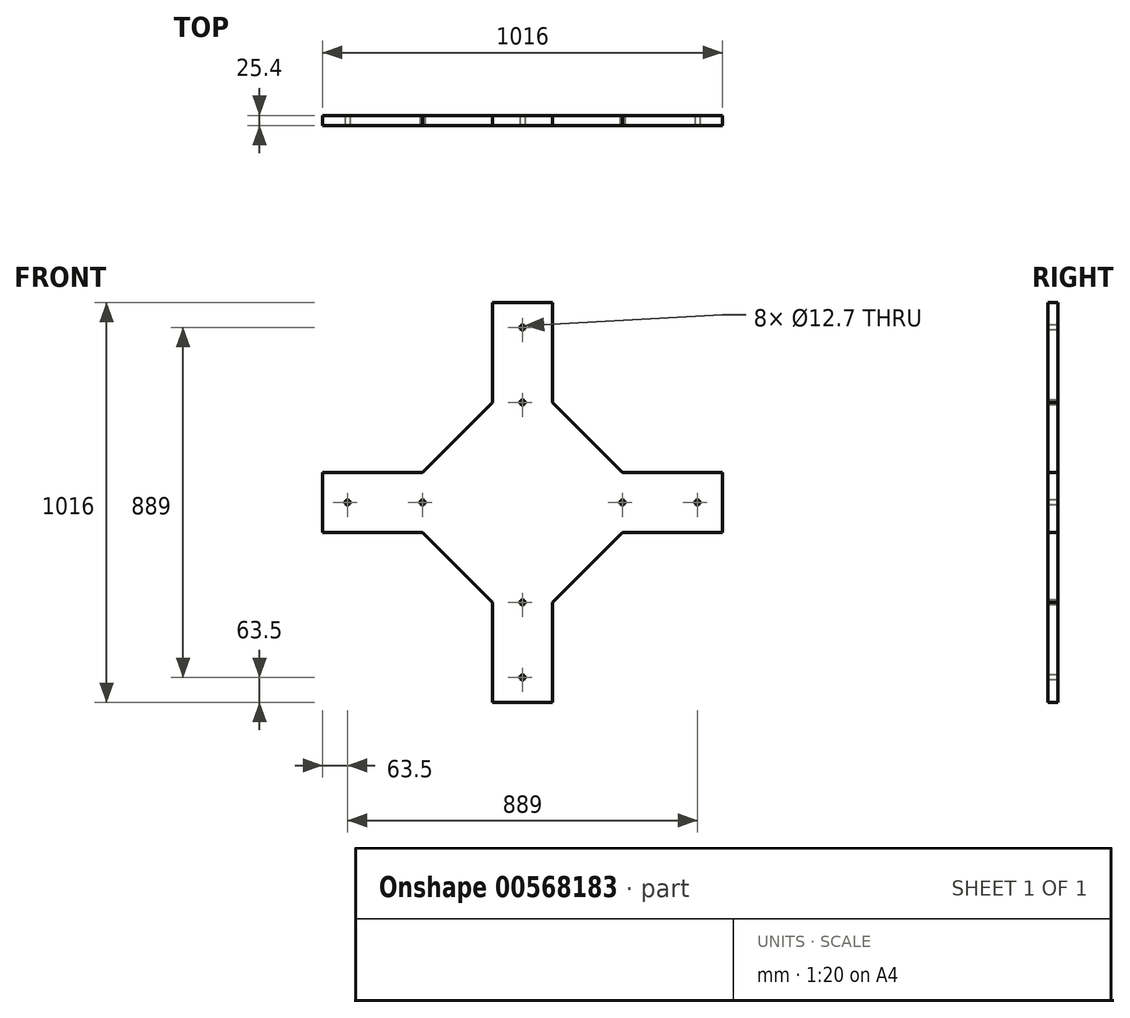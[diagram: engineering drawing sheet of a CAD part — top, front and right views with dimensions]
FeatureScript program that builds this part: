
annotation { "Feature Type Name" : "Feature", "Feature Type Description" : "" }
export const myFeature = defineFeature(function(context is Context, id is Id, definition is map)
    precondition{}
    {
        {
            var Q0;
            Q0=qCreatedBy(makeId("Front.planeOp"),FACE);
            var sketch = newSketch(context, id + "F0", { "sketchPlane" : qUnion([Q0])});
            skLineSegment(sketch, "E0", {"start": v(0, 0) * mm, "end": v(0, -508) * mm});
            skLineSegment(sketch, "E1", {"start": v(0, 0) * mm, "end": v(0, 508) * mm});
            skLineSegment(sketch, "E2", {"start": v(0, 0) * mm, "end": v(508, 0) * mm});
            skLineSegment(sketch, "E3", {"start": v(508, 0) * mm, "end": v(508, 76.2) * mm});
            skLineSegment(sketch, "E4", {"start": v(508, 76.2) * mm, "end": v(508, -76.2) * mm});
            skPoint(sketch, "E4.endSnap0", {"position": v(508, 38.1) * mm});
            skLineSegment(sketch, "E5", {"start": v(0, -508) * mm, "end": v(-76.2, -508) * mm});
            skLineSegment(sketch, "E6", {"start": v(-76.2, -508) * mm, "end": v(76.2, -508) * mm});
            skLineSegment(sketch, "E7", {"start": v(0, 508) * mm, "end": v(-76.2, 508) * mm});
            skLineSegment(sketch, "E8", {"start": v(-76.2, 508) * mm, "end": v(76.2, 508) * mm});
            skLineSegment(sketch, "E9", {"start": v(76.2, 508) * mm, "end": v(76.2, 254) * mm});
            skLineSegment(sketch, "E10", {"start": v(508, 76.2) * mm, "end": v(254, 76.2) * mm});
            skLineSegment(sketch, "E11", {"start": v(508, -76.2) * mm, "end": v(254, -76.2) * mm});
            skLineSegment(sketch, "E12", {"start": v(76.2, -508) * mm, "end": v(76.2, -254) * mm});
            skLineSegment(sketch, "E13", {"start": v(76.2, 254) * mm, "end": v(254, 76.2) * mm});
            skLineSegment(sketch, "E14", {"start": v(254, -76.2) * mm, "end": v(76.2, -254) * mm});
            skLineSegment(sketch, "E15.MirrorCS", {"start": v(-76.2, 508) * mm, "end": v(-76.2, 254) * mm});
            skLineSegment(sketch, "E16.MirrorCS", {"start": v(-76.2, 254) * mm, "end": v(-254, 76.2) * mm});
            skLineSegment(sketch, "E17.MirrorCS", {"start": v(-508, 76.2) * mm, "end": v(-254, 76.2) * mm});
            skLineSegment(sketch, "E18.MirrorCS", {"start": v(-508, 76.2) * mm, "end": v(-508, -76.2) * mm});
            skLineSegment(sketch, "E19.MirrorCS", {"start": v(-508, -76.2) * mm, "end": v(-254, -76.2) * mm});
            skLineSegment(sketch, "E20.MirrorCS", {"start": v(-254, -76.2) * mm, "end": v(-76.2, -254) * mm});
            skLineSegment(sketch, "E21.MirrorCS", {"start": v(-76.2, -508) * mm, "end": v(-76.2, -254) * mm});
            skSolve(sketch);
        }
        {
            var Q0;
            {var subQ1=sQuery(id+"F0.wireOp",EDGE,"E0");Q0=makeQuery(id+"F0.imprint","IMPRINT",FACE,{"disambiguationData":[TD([[makeQuery(id+"F0.imprint","IMPRINT",EDGE,{"derivedFrom":subQ1}),-1.0]])]});}
            var Q1;
            {var subQ1=sQuery(id+"F0.wireOp",EDGE,"E1");Q1=makeQuery(id+"F0.imprint","IMPRINT",FACE,{"disambiguationData":[TD([[makeQuery(id+"F0.imprint","IMPRINT",EDGE,{"derivedFrom":subQ1}),-1.0]])]});}
            var Q2;
            {var subQ1=sQuery(id+"F0.wireOp",EDGE,"E0");Q2=makeQuery(id+"F0.imprint","IMPRINT",FACE,{"disambiguationData":[TD([[makeQuery(id+"F0.imprint","IMPRINT",EDGE,{"derivedFrom":subQ1}),1.0]])]});}
            extrude(context, id + "F1", {"entities" : qUnion([Q0, Q1, Q2]), "depth" : 25.4 * mm, "offsetDistance" : 25.4 * mm});
        }
        {
            var Q0;
            Q0=makeQuery(id+"F1.opExtrude","CAP_FACE",FACE,{"disambiguationData":[OSD([sQuery(id+"F0.wireOp",EDGE,"E4"),sQuery(id+"F0.wireOp",EDGE,"E6"),sQuery(id+"F0.wireOp",EDGE,"E8"),sQuery(id+"F0.wireOp",EDGE,"E9"),sQuery(id+"F0.wireOp",EDGE,"E10"),sQuery(id+"F0.wireOp",EDGE,"E11"),sQuery(id+"F0.wireOp",EDGE,"E12"),sQuery(id+"F0.wireOp",EDGE,"E13"),sQuery(id+"F0.wireOp",EDGE,"E14"),sQuery(id+"F0.wireOp",EDGE,"E15.MirrorCS"),sQuery(id+"F0.wireOp",EDGE,"E16.MirrorCS"),sQuery(id+"F0.wireOp",EDGE,"E17.MirrorCS"),sQuery(id+"F0.wireOp",EDGE,"E18.MirrorCS"),sQuery(id+"F0.wireOp",EDGE,"E19.MirrorCS"),sQuery(id+"F0.wireOp",EDGE,"E20.MirrorCS"),sQuery(id+"F0.wireOp",EDGE,"E21.MirrorCS")])],"isStart":false});
            var sketch = newSketch(context, id + "F2", { "sketchPlane" : qUnion([Q0])});
            skLineSegment(sketch, "E22", {"start": v(0, 0) * mm, "end": v(-508, 0) * mm});
            skLineSegment(sketch, "E23", {"start": v(-508, 0) * mm, "end": v(0, 0) * mm});
            skLineSegment(sketch, "E24", {"start": v(508, 0) * mm, "end": v(0, 0) * mm});
            skLineSegment(sketch, "E25", {"start": v(0, 0) * mm, "end": v(0, 508) * mm});
            skLineSegment(sketch, "E26", {"start": v(0, 508) * mm, "end": v(0, 0) * mm});
            skLineSegment(sketch, "E27", {"start": v(0, 0) * mm, "end": v(0, -508) * mm});
            skPoint(sketch, "E28", {"position": v(-444.5, 0) * mm});
            skPoint(sketch, "E29", {"position": v(-820.91, 430.72) * mm});
            skPoint(sketch, "E30", {"position": v(-254, 0) * mm});
            skPoint(sketch, "E31", {"position": v(0, 444.5) * mm});
            skPoint(sketch, "E32", {"position": v(0, 254) * mm});
            skPoint(sketch, "E33", {"position": v(444.5, 0) * mm});
            skPoint(sketch, "E34", {"position": v(254, 0) * mm});
            skPoint(sketch, "E35", {"position": v(0, -254) * mm});
            skPoint(sketch, "E36", {"position": v(0, -444.5) * mm});
            skCircle(sketch, "E37", {"center": v(0, 0) * mm, "radius": 25.4 * mm});
            skCircle(sketch, "E38", {"center": v(-444.5, 0) * mm, "radius": 6.35 * mm});
            skCircle(sketch, "E39", {"center": v(-254, 0) * mm, "radius": 6.35 * mm});
            skCircle(sketch, "E40", {"center": v(0, -254) * mm, "radius": 6.35 * mm});
            skCircle(sketch, "E41", {"center": v(0, -444.5) * mm, "radius": 6.35 * mm});
            skCircle(sketch, "E42", {"center": v(0, 254) * mm, "radius": 6.35 * mm});
            skCircle(sketch, "E43", {"center": v(0, 444.5) * mm, "radius": 6.35 * mm});
            skCircle(sketch, "E44", {"center": v(444.5, 0) * mm, "radius": 6.35 * mm});
            skCircle(sketch, "E45", {"center": v(254, 0) * mm, "radius": 6.35 * mm});
            skSolve(sketch);
        }
        {
            var Q0;
            Q0=sQuery(id+"F2.wireOp",VERTEX,"E31");
            var Q1;
            Q1=sQuery(id+"F2.wireOp",VERTEX,"E32");
            var Q2;
            Q2=sQuery(id+"F2.wireOp",VERTEX,"E45.center");
            var Q3;
            Q3=sQuery(id+"F2.wireOp",VERTEX,"E33");
            var Q4;
            Q4=sQuery(id+"F2.wireOp",VERTEX,"E35");
            var Q5;
            Q5=sQuery(id+"F2.wireOp",VERTEX,"E36");
            var Q6;
            Q6=sQuery(id+"F2.wireOp",VERTEX,"E30");
            var Q7;
            Q7=sQuery(id+"F2.wireOp",VERTEX,"E28");
            var Q8;
            Q8=makeQuery(id+"F1.opExtrude","SWEPT_BODY",BODY,{"disambiguationData":[OSD([sQuery(id+"F0.wireOp",EDGE,"E4"),sQuery(id+"F0.wireOp",EDGE,"E6"),sQuery(id+"F0.wireOp",EDGE,"E8"),sQuery(id+"F0.wireOp",EDGE,"E9"),sQuery(id+"F0.wireOp",EDGE,"E10"),sQuery(id+"F0.wireOp",EDGE,"E11"),sQuery(id+"F0.wireOp",EDGE,"E12"),sQuery(id+"F0.wireOp",EDGE,"E13"),sQuery(id+"F0.wireOp",EDGE,"E14"),sQuery(id+"F0.wireOp",EDGE,"E15.MirrorCS"),sQuery(id+"F0.wireOp",EDGE,"E16.MirrorCS"),sQuery(id+"F0.wireOp",EDGE,"E17.MirrorCS"),sQuery(id+"F0.wireOp",EDGE,"E18.MirrorCS"),sQuery(id+"F0.wireOp",EDGE,"E19.MirrorCS"),sQuery(id+"F0.wireOp",EDGE,"E20.MirrorCS"),sQuery(id+"F0.wireOp",EDGE,"E21.MirrorCS")])]});
            hole(context, id + "F3", {"style" : HoleStyle.SIMPLE, "endStyle" : HoleEndStyle.THROUGH, "holeDiameter" : 12.7 * mm, "isTappedThrough" : true, "tappedDepth" : 12.7 * mm, "tapClearance" : 3, "locations" : qUnion([Q0, Q1, Q2, Q3, Q4, Q5, Q6, Q7]), "scope" : qUnion([Q8])});
        }
    });
